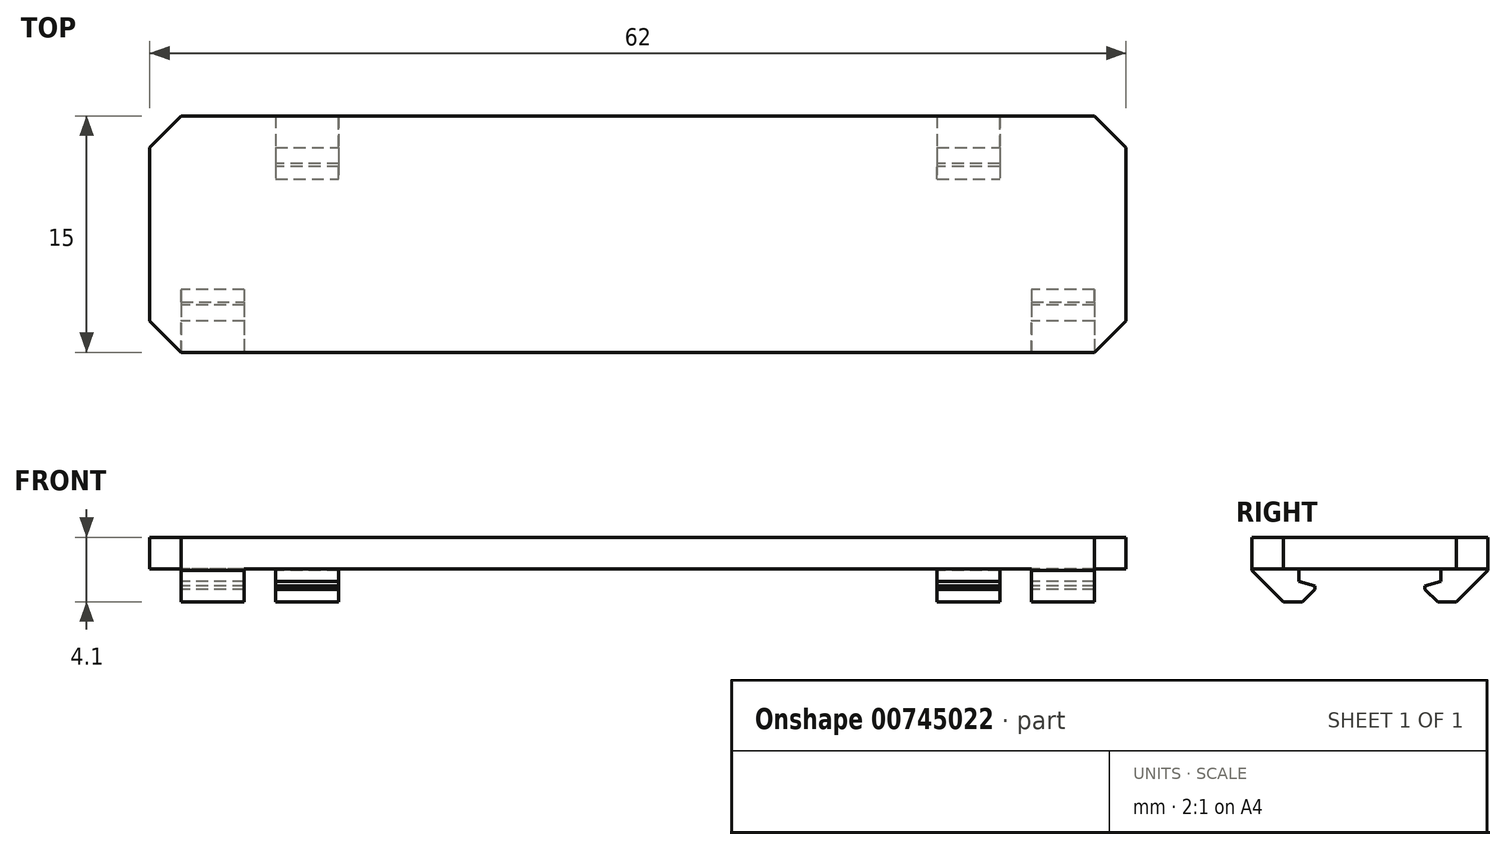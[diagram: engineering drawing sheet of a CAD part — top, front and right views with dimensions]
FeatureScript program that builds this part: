
annotation { "Feature Type Name" : "Feature", "Feature Type Description" : "" }
export const myFeature = defineFeature(function(context is Context, id is Id, definition is map)
    precondition{}
    {
        {
            var Q0;
            Q0=qCreatedBy(makeId("Top.planeOp"),FACE);
            var sketch = newSketch(context, id + "F0", { "sketchPlane" : qUnion([Q0])});
            skLineSegment(sketch, "E0.bottom", {"start": v(31, -7.5) * mm, "end": v(-31, -7.5) * mm});
            skLineSegment(sketch, "E0.top", {"start": v(31, 7.5) * mm, "end": v(-31, 7.5) * mm});
            skLineSegment(sketch, "E0.left", {"start": v(31, -7.5) * mm, "end": v(31, 7.5) * mm});
            skLineSegment(sketch, "E0.right", {"start": v(-31, -7.5) * mm, "end": v(-31, 7.5) * mm});
            skPoint(sketch, "E0.middle", {"position": v(0, 0) * mm});
            skSolve(sketch);
        }
        {
            var Q0;
            Q0=makeQuery(id+"F0.imprint","IMPRINT",FACE,{"disambiguationData":[TD([[makeQuery(id+"F0.imprint","IMPRINT",EDGE,{"derivedFrom":sQuery(id+"F0.wireOp",EDGE,"E0.bottom")}),-1.0]])]});
            extrude(context, id + "F1", {"entities" : qUnion([Q0]), "depth" : 2 * mm, "offsetDistance" : 25 * mm});
        }
        {
            var Q0;
            Q0=makeQuery(id+"F1.opExtrude","CAP_FACE",FACE,{"disambiguationData":[OSD([sQuery(id+"F0.wireOp",EDGE,"E0.bottom"),sQuery(id+"F0.wireOp",EDGE,"E0.top"),sQuery(id+"F0.wireOp",EDGE,"E0.left"),sQuery(id+"F0.wireOp",EDGE,"E0.right")])],"isStart":true});
            var sketch = newSketch(context, id + "F2", { "sketchPlane" : qUnion([Q0])});
            skLineSegment(sketch, "E1.bottom", {"start": v(-25, 4.5) * mm, "end": v(-29, 4.5) * mm});
            skLineSegment(sketch, "E1.top", {"start": v(-25, 7.5) * mm, "end": v(-29, 7.5) * mm});
            skLineSegment(sketch, "E1.left", {"start": v(-25, 4.5) * mm, "end": v(-25, 7.5) * mm});
            skLineSegment(sketch, "E1.right", {"start": v(-29, 4.5) * mm, "end": v(-29, 7.5) * mm});
            skPoint(sketch, "E1.middle", {"position": v(-27, 6) * mm});
            skLineSegment(sketch, "E2.MirrorCS", {"start": v(25, 7.5) * mm, "end": v(29, 7.5) * mm});
            skLineSegment(sketch, "E3.MirrorCS", {"start": v(29, 4.5) * mm, "end": v(29, 7.5) * mm});
            skLineSegment(sketch, "E4.MirrorCS", {"start": v(25, 4.5) * mm, "end": v(29, 4.5) * mm});
            skLineSegment(sketch, "E5.MirrorCS", {"start": v(25, 4.5) * mm, "end": v(25, 7.5) * mm});
            skLineSegment(sketch, "E6.bottom", {"start": v(-19, -7.5) * mm, "end": v(-23, -7.5) * mm});
            skLineSegment(sketch, "E6.top", {"start": v(-19, -4.5) * mm, "end": v(-23, -4.5) * mm});
            skLineSegment(sketch, "E6.left", {"start": v(-19, -7.5) * mm, "end": v(-19, -4.5) * mm});
            skLineSegment(sketch, "E6.right", {"start": v(-23, -7.5) * mm, "end": v(-23, -4.5) * mm});
            skPoint(sketch, "E6.middle", {"position": v(-21, -6) * mm});
            skLineSegment(sketch, "E7.MirrorCS", {"start": v(19, -4.5) * mm, "end": v(23, -4.5) * mm});
            skLineSegment(sketch, "E8.MirrorCS", {"start": v(23, -7.5) * mm, "end": v(23, -4.5) * mm});
            skLineSegment(sketch, "E9.MirrorCS", {"start": v(19, -7.5) * mm, "end": v(19, -4.5) * mm});
            skLineSegment(sketch, "E10.MirrorCS", {"start": v(19, -7.5) * mm, "end": v(23, -7.5) * mm});
            skSolve(sketch);
        }
        {
            var Q0;
            Q0=makeQuery(id+"F2.imprint","IMPRINT",FACE,{"disambiguationData":[TD([[makeQuery(id+"F2.imprint","IMPRINT",EDGE,{"derivedFrom":sQuery(id+"F2.wireOp",EDGE,"E1.bottom")}),-1.0]])]});
            var Q1;
            Q1=makeQuery(id+"F2.imprint","IMPRINT",FACE,{"disambiguationData":[TD([[makeQuery(id+"F2.imprint","IMPRINT",EDGE,{"derivedFrom":sQuery(id+"F2.wireOp",EDGE,"E6.bottom")}),-1.0]])]});
            var Q2;
            Q2=makeQuery(id+"F2.imprint","IMPRINT",FACE,{"disambiguationData":[TD([[makeQuery(id+"F2.imprint","IMPRINT",EDGE,{"derivedFrom":sQuery(id+"F2.wireOp",EDGE,"E7.MirrorCS")}),-1.0]])]});
            var Q3;
            Q3=makeQuery(id+"F2.imprint","IMPRINT",FACE,{"disambiguationData":[TD([[makeQuery(id+"F2.imprint","IMPRINT",EDGE,{"derivedFrom":sQuery(id+"F2.wireOp",EDGE,"E2.MirrorCS")}),1.0]])]});
            extrude(context, id + "F3", {"entities" : qUnion([Q0, Q1, Q2, Q3]), "operationType" : NewBodyOperationType.ADD, "depth" : 2.1 * mm, "offsetDistance" : 25 * mm});
        }
        {
            var Q0;
            Q0=makeQuery(id+"F1.opExtrude","SWEPT_EDGE",EDGE,{"disambiguationData":[OSD([sQuery(id+"F0.wireOp",EDGE,"E0.bottom"),sQuery(id+"F0.wireOp",EDGE,"E0.right")])]});
            var Q1;
            Q1=makeQuery(id+"F1.opExtrude","SWEPT_EDGE",EDGE,{"disambiguationData":[OSD([sQuery(id+"F0.wireOp",EDGE,"E0.top"),sQuery(id+"F0.wireOp",EDGE,"E0.right")])]});
            var Q2;
            Q2=makeQuery(id+"F3.opExtrude","CAP_EDGE",EDGE,{"disambiguationData":[OSD([sQuery(id+"F2.wireOp",EDGE,"E6.bottom")])],"isStart":false});
            var Q3;
            Q3=makeQuery(id+"F3.opExtrude","CAP_EDGE",EDGE,{"disambiguationData":[OSD([sQuery(id+"F2.wireOp",EDGE,"E1.top")])],"isStart":false});
            var Q4;
            Q4=makeQuery(id+"F1.opExtrude","SWEPT_EDGE",EDGE,{"disambiguationData":[OSD([sQuery(id+"F0.wireOp",EDGE,"E0.bottom"),sQuery(id+"F0.wireOp",EDGE,"E0.left")])]});
            var Q5;
            Q5=makeQuery(id+"F3.opExtrude","CAP_EDGE",EDGE,{"disambiguationData":[OSD([sQuery(id+"F2.wireOp",EDGE,"E2.MirrorCS")])],"isStart":false});
            var Q6;
            Q6=makeQuery(id+"F1.opExtrude","SWEPT_EDGE",EDGE,{"disambiguationData":[OSD([sQuery(id+"F0.wireOp",EDGE,"E0.top"),sQuery(id+"F0.wireOp",EDGE,"E0.left")])]});
            var Q7;
            Q7=makeQuery(id+"F3.opExtrude","CAP_EDGE",EDGE,{"disambiguationData":[OSD([sQuery(id+"F2.wireOp",EDGE,"E10.MirrorCS")])],"isStart":false});
            chamfer(context, id + "F4", {"entities" : qUnion([Q0, Q1, Q2, Q3, Q4, Q5, Q6, Q7]), "width" : 2 * mm, "tangentPropagation" : true});
        }
        {
            var Q0;
            Q0=makeQuery(id+"F3.opExtrude","SWEPT_FACE",FACE,{"disambiguationData":[OSD([sQuery(id+"F2.wireOp",EDGE,"E1.bottom")])]});
            var Q1;
            Q1=makeQuery(id+"F3.opExtrude","SWEPT_FACE",FACE,{"disambiguationData":[OSD([sQuery(id+"F2.wireOp",EDGE,"E4.MirrorCS")])]});
            var Q2;
            Q2=makeQuery(id+"F3.opExtrude","SWEPT_FACE",FACE,{"disambiguationData":[OSD([sQuery(id+"F2.wireOp",EDGE,"E7.MirrorCS")])]});
            var Q3;
            Q3=makeQuery(id+"F3.opExtrude","SWEPT_FACE",FACE,{"disambiguationData":[OSD([sQuery(id+"F2.wireOp",EDGE,"E6.top")])]});
            extrude(context, id + "F5", {"entities" : qUnion([Q0, Q1, Q2, Q3]), "operationType" : NewBodyOperationType.ADD, "endBound" : BoundingType.SYMMETRIC, "depth" : 2 * mm, "offsetDistance" : 25 * mm});
        }
        {
            var Q0;
            {var subQ0=sQuery(id+"F2.wireOp",EDGE,"E1.right");Q0=makeQuery(id+"F5.boolean.opBoolean","MERGE",FACE,{"derivedFrom":[makeQuery(id+"F3.opExtrude","SWEPT_FACE",FACE,{"disambiguationData":[OSD([subQ0])]}),makeQuery(id+"F5.opExtrude","SWEPT_FACE",FACE,{"disambiguationData":[OSD([sQuery(id+"F2.wireOp",EDGE,"E1.bottom"),subQ0])]})]});}
            var sketch = newSketch(context, id + "F6", { "sketchPlane" : qUnion([Q0])});
            skLineSegment(sketch, "E11", {"start": v(3.5, 0) * mm, "end": v(4.5, 0) * mm});
            skLineSegment(sketch, "E12", {"start": v(4.5, 0) * mm, "end": v(4.5, -0.8) * mm});
            skPoint(sketch, "E13.endSnap0", {"position": v(3.5, -1.05) * mm});
            skLineSegment(sketch, "E14", {"start": v(3.5, -1.1) * mm, "end": v(4.5, -0.8) * mm});
            skLineSegment(sketch, "E15", {"start": v(3.5, -1.1) * mm, "end": v(3.5, -1.9) * mm});
            skPoint(sketch, "E16.start.orphan", {"position": v(3.5, -0.8) * mm});
            skSolve(sketch);
        }
        {
            var Q0;
            {var subQ0=sQuery(id+"F6.wireOp",EDGE,"E11");Q0=makeQuery(id+"F6.imprint","IMPRINT",FACE,{"disambiguationData":[TD([[makeQuery(id+"F6.imprint","IMPRINT",EDGE,{"derivedFrom":subQ0}),-1.0]])]});}
            extrude(context, id + "F7", {"entities" : qUnion([Q0]), "oppositeDirection" : true, "depth" : 70 * mm, "offsetDistance" : 25 * mm});
        }
        {
            var Q0;
            Q0=makeQuery(id+"F7.opExtrude","SWEPT_BODY",BODY,{"disambiguationData":[OSD([sQuery(id+"F2.wireOp",EDGE,"E1.bottom"),sQuery(id+"F2.wireOp",EDGE,"E1.right"),sQuery(id+"F6.wireOp",EDGE,"E11"),sQuery(id+"F6.wireOp",EDGE,"E12"),sQuery(id+"F6.wireOp",EDGE,"E14")])]});
            var Q1;
            Q1=qCreatedBy(makeId("Front.planeOp"),FACE);
            mirror(context, id + "F8", {"entities" : qUnion([Q0]), "mirrorPlane" : qUnion([Q1])});
        }
        {
            var Q0;
            Q0=makeQuery(id+"F7.opExtrude","SWEPT_BODY",BODY,{"disambiguationData":[OSD([sQuery(id+"F2.wireOp",EDGE,"E1.bottom"),sQuery(id+"F2.wireOp",EDGE,"E1.right"),sQuery(id+"F6.wireOp",EDGE,"E11"),sQuery(id+"F6.wireOp",EDGE,"E12"),sQuery(id+"F6.wireOp",EDGE,"E14")])]});
            var Q1;
            Q1=makeQuery(id+"F8.opPattern","COPY",BODY,{"derivedFrom":makeQuery(id+"F7.opExtrude","SWEPT_BODY",BODY,{"disambiguationData":[OSD([sQuery(id+"F2.wireOp",EDGE,"E1.bottom"),sQuery(id+"F2.wireOp",EDGE,"E1.right"),sQuery(id+"F6.wireOp",EDGE,"E11"),sQuery(id+"F6.wireOp",EDGE,"E12"),sQuery(id+"F6.wireOp",EDGE,"E14")])]}),"instanceName":"1"});
            var Q2;
            Q2=makeQuery(id+"F1.opExtrude","SWEPT_BODY",BODY,{"disambiguationData":[OSD([sQuery(id+"F0.wireOp",EDGE,"E0.bottom"),sQuery(id+"F0.wireOp",EDGE,"E0.top"),sQuery(id+"F0.wireOp",EDGE,"E0.left"),sQuery(id+"F0.wireOp",EDGE,"E0.right")])]});
            booleanBodies(context, id + "F9", {"operationType" : BooleanOperationType.SUBTRACTION, "tools" : qUnion([Q0, Q1]), "targets" : qUnion([Q2])});
        }
        {
            var Q0;
            {var subQ0=sQuery(id+"F2.wireOp",EDGE,"E1.bottom");Q0=makeQuery(id+"F5.opExtrude","CAP_EDGE",EDGE,{"disambiguationData":[OSD([subQ0]),TDD([makeQuery(id+"F3.opExtrude","CAP_EDGE",EDGE,{"disambiguationData":[OSD([subQ0])],"isStart":false})])],"isStart":false});}
            var Q1;
            {var subQ0=sQuery(id+"F2.wireOp",EDGE,"E4.MirrorCS");Q1=makeQuery(id+"F5.opExtrude","CAP_EDGE",EDGE,{"disambiguationData":[OSD([subQ0]),TDD([makeQuery(id+"F3.opExtrude","CAP_EDGE",EDGE,{"disambiguationData":[OSD([subQ0])],"isStart":false})])],"isStart":false});}
            var Q2;
            {var subQ0=sQuery(id+"F2.wireOp",EDGE,"E7.MirrorCS");Q2=makeQuery(id+"F5.opExtrude","CAP_EDGE",EDGE,{"disambiguationData":[OSD([subQ0]),TDD([makeQuery(id+"F3.opExtrude","CAP_EDGE",EDGE,{"disambiguationData":[OSD([subQ0])],"isStart":false})])],"isStart":true});}
            var Q3;
            {var subQ0=sQuery(id+"F2.wireOp",EDGE,"E6.top");Q3=makeQuery(id+"F5.opExtrude","CAP_EDGE",EDGE,{"disambiguationData":[OSD([subQ0]),TDD([makeQuery(id+"F3.opExtrude","CAP_EDGE",EDGE,{"disambiguationData":[OSD([subQ0])],"isStart":false})])],"isStart":true});}
            chamfer(context, id + "F10", {"entities" : qUnion([Q0, Q1, Q2, Q3]), "width" : 0.8 * mm, "tangentPropagation" : true});
        }
    });
